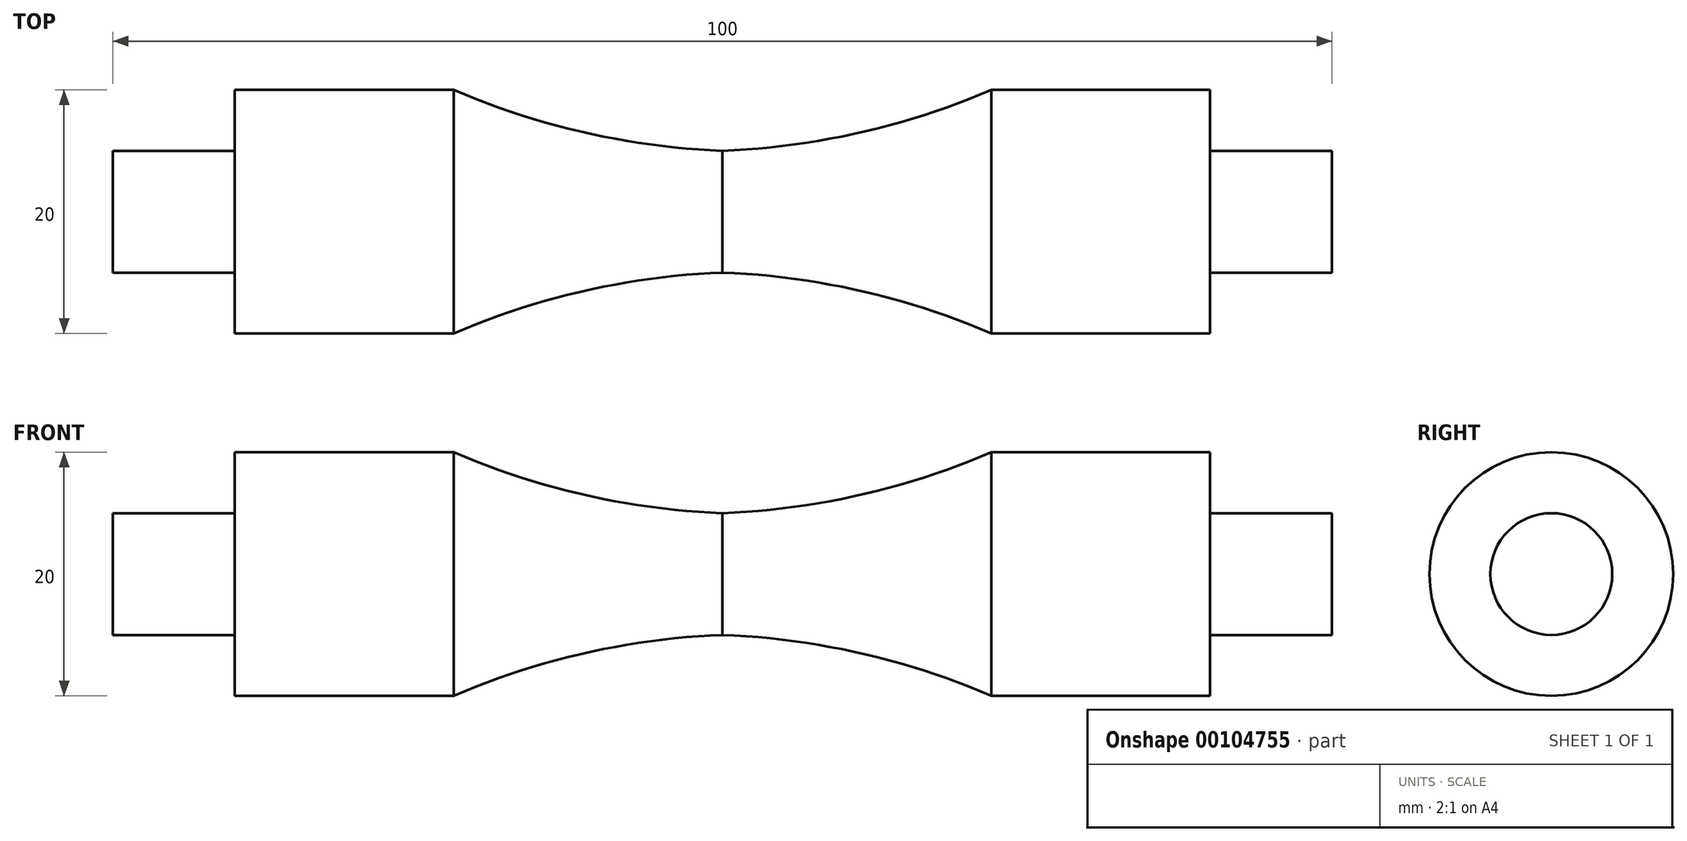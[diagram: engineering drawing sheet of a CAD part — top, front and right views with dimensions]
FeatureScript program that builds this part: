
annotation { "Feature Type Name" : "Feature", "Feature Type Description" : "" }
export const myFeature = defineFeature(function(context is Context, id is Id, definition is map)
    precondition{}
    {
        {
            var Q0;
            Q0=qCreatedBy(makeId("Front.planeOp"),FACE);
            var sketch = newSketch(context, id + "F0", { "sketchPlane" : qUnion([Q0])});
            skLineSegment(sketch, "E0", {"start": v(-24.85, 0) * mm, "end": v(-24.85, 5) * mm});
            skLineSegment(sketch, "E1", {"start": v(-24.85, 5) * mm, "end": v(-14.85, 5) * mm});
            skLineSegment(sketch, "E2", {"start": v(-14.85, 5) * mm, "end": v(-14.85, 10) * mm});
            skLineSegment(sketch, "E3", {"start": v(-14.85, 10) * mm, "end": v(3.1, 10) * mm});
            skLineSegment(sketch, "E4", {"start": v(25.15, 5) * mm, "end": v(25.15, 0) * mm});
            skLineSegment(sketch, "E5", {"start": v(25.15, 0) * mm, "end": v(-24.85, 0) * mm});
            skArc(sketch, "E6", {"start": v(3.1, 10) * mm, "mid": v(13.9, 6.48) * mm, "end": v(25.15, 5) * mm});
            skPoint(sketch, "E7.orphan", {"position": v(25.15, 10) * mm});
            skSolve(sketch);
        }
        {
            var Q0;
            Q0=makeQuery(id+"F0.imprint","IMPRINT",FACE,{"disambiguationData":[TD([[makeQuery(id+"F0.imprint","IMPRINT",EDGE,{"derivedFrom":sQuery(id+"F0.wireOp",EDGE,"E0")}),-1.0]])]});
            var Q1;
            Q1=sQuery(id+"F0.wireOp",EDGE,"E5");
            revolve(context, id + "F1", {"entities" : qUnion([Q0]), "axis" : qUnion([Q1]), "revolveType" : RevolveType.FULL});
        }
        {
            var Q0;
            Q0=makeQuery(id+"F1.opRevolve","SWEPT_BODY",BODY,{"disambiguationData":[OSD([sQuery(id+"F0.wireOp",EDGE,"E0"),sQuery(id+"F0.wireOp",EDGE,"E1"),sQuery(id+"F0.wireOp",EDGE,"E2"),sQuery(id+"F0.wireOp",EDGE,"E3"),sQuery(id+"F0.wireOp",EDGE,"E4"),sQuery(id+"F0.wireOp",EDGE,"E5"),sQuery(id+"F0.wireOp",EDGE,"E6")])]});
            var Q1;
            Q1=makeQuery(id+"F1.opRevolve","SWEPT_FACE",FACE,{"disambiguationData":[OSD([sQuery(id+"F0.wireOp",EDGE,"E4")])]});
            mirror(context, id + "F2", {"entities" : qUnion([Q0]), "mirrorPlane" : qUnion([Q1])});
        }
    });
